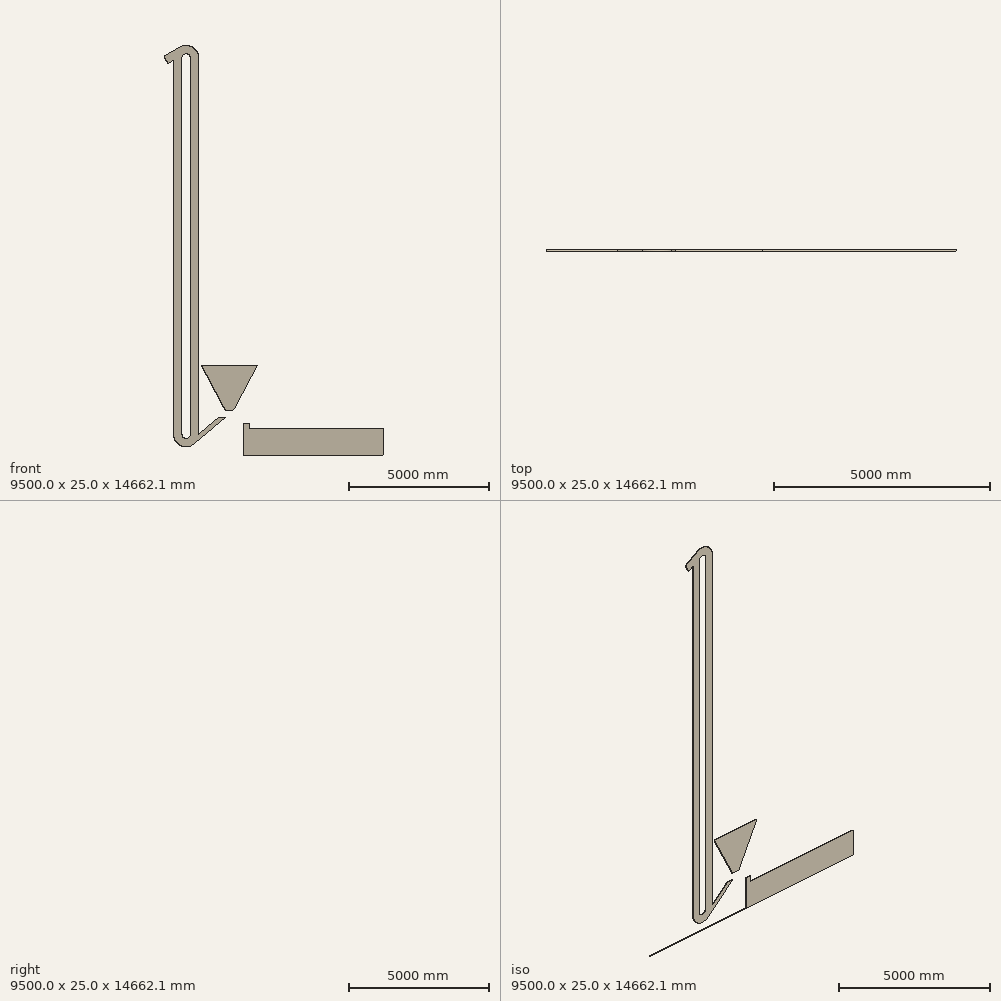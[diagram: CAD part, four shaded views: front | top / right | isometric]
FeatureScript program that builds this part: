
annotation { "Feature Type Name" : "Feature", "Feature Type Description" : "" }
export const myFeature = defineFeature(function(context is Context, id is Id, definition is map)
    precondition{}
    {
        {
            var Q0;
            Q0=qCreatedBy(makeId("Front.planeOp"),FACE);
            var sketch = newSketch(context, id + "F0", { "sketchPlane" : qUnion([Q0])});
            skLineSegment(sketch, "E0", {"start": v(0, 3200) * mm, "end": v(850, 1600) * mm});
            skLineSegment(sketch, "E1", {"start": v(850, 1600) * mm, "end": v(1150, 1600) * mm});
            skLineSegment(sketch, "E2", {"start": v(1150, 1600) * mm, "end": v(2000, 3200) * mm});
            skLineSegment(sketch, "E3", {"start": v(2000, 3200) * mm, "end": v(0, 3200) * mm});
            skLineSegment(sketch, "E4", {"start": v(-3000, 0) * mm, "end": v(1500, 0) * mm});
            skLineSegment(sketch, "E5", {"start": v(-100, 14202.07) * mm, "end": v(-100, 744.23) * mm});
            skLineSegment(sketch, "E6", {"start": v(-100, 744.23) * mm, "end": v(0, 828.14) * mm});
            skLineSegment(sketch, "E7", {"start": v(0, 828.14) * mm, "end": v(103.33, 705) * mm});
            skLineSegment(sketch, "E8", {"start": v(103.33, 705) * mm, "end": v(-260.75, 399.5) * mm});
            skLineSegment(sketch, "E9", {"start": v(-1000, 744.23) * mm, "end": v(-1000, 14115.47) * mm});
            skArc(sketch, "E10", {"start": v(-260.75, 399.5) * mm, "mid": v(-740.18, 336.39) * mm, "end": v(-1000, 744.23) * mm});
            skArc(sketch, "E11", {"start": v(-400, 744.23) * mm, "mid": v(-550, 594.23) * mm, "end": v(-700, 744.23) * mm});
            skLineSegment(sketch, "E12", {"start": v(-700, 744.23) * mm, "end": v(-700, 14202.07) * mm});
            skLineSegment(sketch, "E13", {"start": v(-400, 744.23) * mm, "end": v(-400, 14202.07) * mm});
            skLineSegment(sketch, "E14", {"start": v(1500, 1150) * mm, "end": v(1700, 1150) * mm});
            skLineSegment(sketch, "E15", {"start": v(1700, 1150) * mm, "end": v(1700, 950) * mm});
            skLineSegment(sketch, "E16", {"start": v(1700, 950) * mm, "end": v(6500, 950) * mm});
            skLineSegment(sketch, "E17", {"start": v(6500, 950) * mm, "end": v(6500, 0) * mm});
            skLineSegment(sketch, "E18", {"start": v(1500, 1150) * mm, "end": v(1500, 0) * mm});
            skArc(sketch, "E19", {"start": v(-775, 14591.78) * mm, "mid": v(-325, 14591.78) * mm, "end": v(-100, 14202.07) * mm});
            skArc(sketch, "E20", {"start": v(-700, 14202.07) * mm, "mid": v(-550, 14352.07) * mm, "end": v(-400, 14202.07) * mm});
            skLineSegment(sketch, "E21", {"start": v(-775, 14591.78) * mm, "end": v(-1350, 14259.8) * mm});
            skLineSegment(sketch, "E22", {"start": v(-1350, 14259.8) * mm, "end": v(-1200, 14000) * mm});
            skLineSegment(sketch, "E23", {"start": v(-1200, 14000) * mm, "end": v(-1000, 14115.47) * mm});
            skLineSegment(sketch, "E24", {"start": v(-3000, 0) * mm, "end": v(-3000, -10) * mm});
            skLineSegment(sketch, "E25", {"start": v(-3000, -10) * mm, "end": v(6500, -10) * mm});
            skLineSegment(sketch, "E26", {"start": v(6500, 0) * mm, "end": v(6500, -10) * mm});
            skPoint(sketch, "E27.orphan", {"position": v(-1000, 14202.07) * mm});
            skLineSegment(sketch, "E28", {"start": v(103.33, 705) * mm, "end": v(872, 1350) * mm});
            skLineSegment(sketch, "E29", {"start": v(621.93, 1350) * mm, "end": v(0, 828.14) * mm});
            skLineSegment(sketch, "E30", {"start": v(621.93, 1350) * mm, "end": v(872, 1350) * mm});
            skSolve(sketch);
        }
        {
            var Q0;
            Q0 = qSketchRegion(id + "F0", true);
            extrude(context, id + "F1", {"entities" : qUnion([Q0]), "depth" : 25 * mm});
        }
    });
